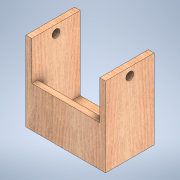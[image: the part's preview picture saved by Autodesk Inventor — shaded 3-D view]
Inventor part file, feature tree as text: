
AUTODESK INVENTOR PART (.ipt)
format: ipt  version: 2022.2 (Build 262287000, 287)  size: 175,104 bytes
history: native  units: in
note: dims shown in document units (in); Inventor stores cm internally (conversion verified against a paired STEP export)
features: sketch x5, extrude x4, hole x1
ambient origin geometry x8: Origin, YZ Plane, XZ Plane, XY Plane, X Axis, Y Axis, Z Axis, Center Point
bodies: Solid1 (feature_tree)
feature tree (10):
  extrude  "Base"  Depth=6.25in
  extrude  "Sides"  Depth=0.75in
  extrude  "FrontPiece"  Depth=0.75in
  hole  "HoleForSides"  [1 undecoded]
  extrude  "BottomHole"  Depth=0.75in
  sketch  "Sketch1"  dims[d0=10.25in d1=6.25in]
  sketch  "Sketch2"  dims[d2=0.75in d3=0.0in d4=0.75in]
  sketch  "Sketch3"  dims[d5=9.5in d6=0.0in d7=0.75in]
  sketch  "Sketch5"  dims[d8=4.5in d9=0.0in]
  sketch  "Sketch8"  dims[d13=1.02in d14=0.75in d15=0.3209in d16=0.292in d17=0.5635in d18=0.3543in d19=0.0in d23=8.5in d27=1.25in d28=1.25in d29=0.0in]
note: 1 required parameter value undecoded (feature->parameter linkage not recoverable at this tier; creation-order binding heuristic only, values carry confidence <= 0.55)
